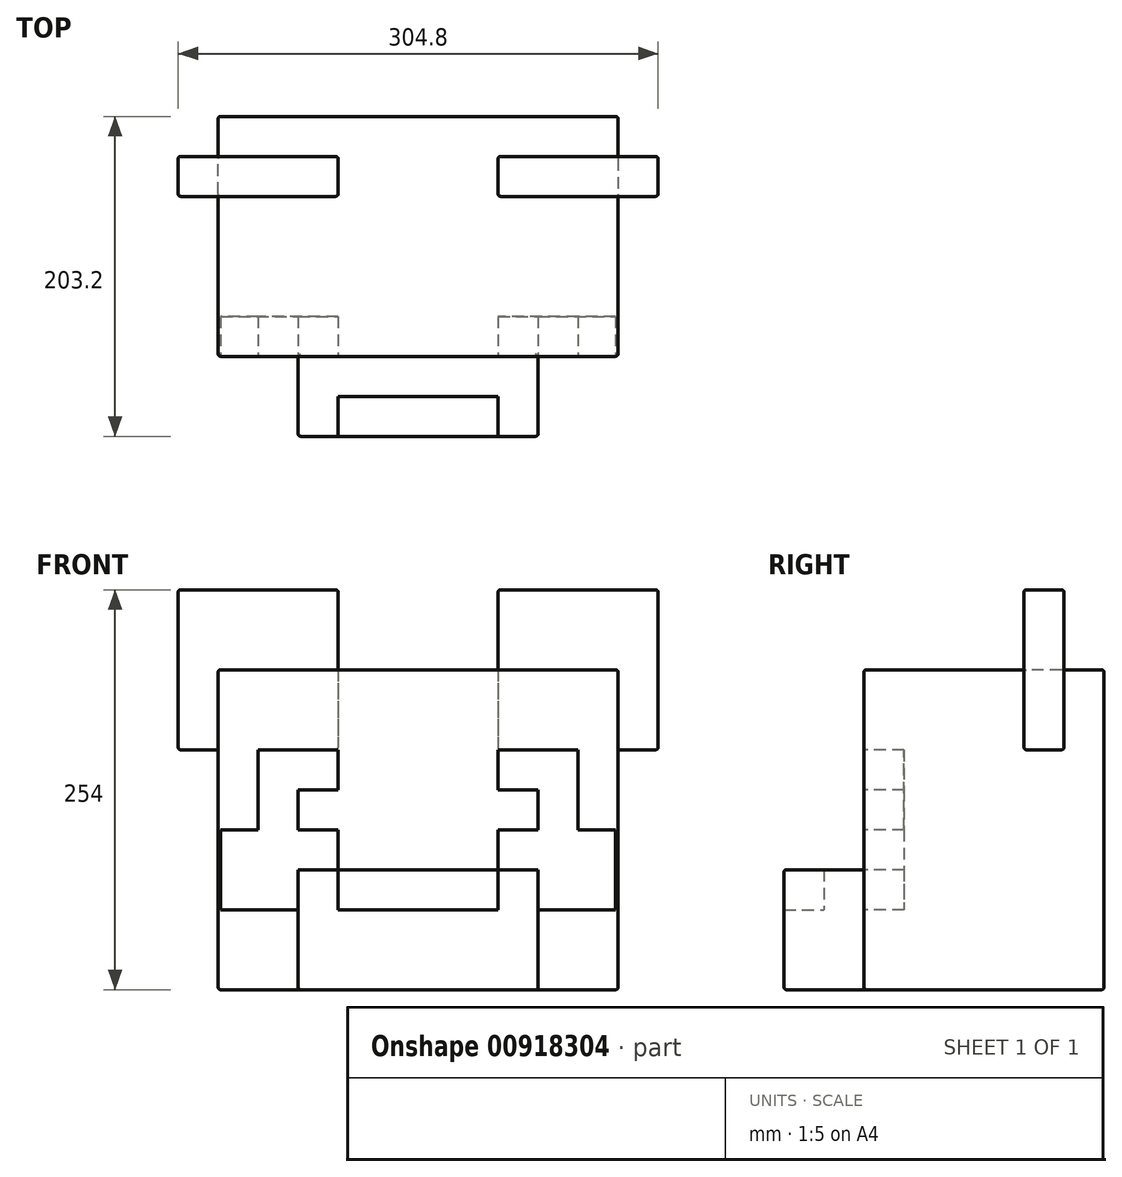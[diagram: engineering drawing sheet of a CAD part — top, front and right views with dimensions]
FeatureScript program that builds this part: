
annotation { "Feature Type Name" : "Feature", "Feature Type Description" : "" }
export const myFeature = defineFeature(function(context is Context, id is Id, definition is map)
    precondition{}
    {
        {
            var Q0;
            Q0=qCreatedBy(makeId("Front.planeOp"),FACE);
            var sketch = newSketch(context, id + "F0", { "sketchPlane" : qUnion([Q0])});
            skLineSegment(sketch, "E0", {"start": v(50.8, 50.8) * mm, "end": v(50.8, 25.4) * mm});
            skLineSegment(sketch, "E1", {"start": v(50.8, 25.4) * mm, "end": v(76.2, 25.4) * mm});
            skLineSegment(sketch, "E2", {"start": v(76.2, 25.4) * mm, "end": v(76.2, 0) * mm});
            skLineSegment(sketch, "E3.bottom", {"start": v(127, 101.6) * mm, "end": v(-127, 101.6) * mm});
            skLineSegment(sketch, "E3.top", {"start": v(127, -101.6) * mm, "end": v(-127, -101.6) * mm});
            skLineSegment(sketch, "E3.left", {"start": v(127, 101.6) * mm, "end": v(127, -101.6) * mm});
            skLineSegment(sketch, "E3.right", {"start": v(-127, 101.6) * mm, "end": v(-127, -101.6) * mm});
            skPoint(sketch, "E3.middle", {"position": v(0, 0) * mm});
            skPoint(sketch, "E4", {"position": v(127, 76.2) * mm});
            skPoint(sketch, "E5", {"position": v(127, 50.8) * mm});
            skPoint(sketch, "E6", {"position": v(127, 25.4) * mm});
            skPoint(sketch, "E7", {"position": v(127, 0) * mm});
            skPoint(sketch, "E8", {"position": v(127, -25.4) * mm});
            skPoint(sketch, "E9", {"position": v(127, -50.8) * mm});
            skPoint(sketch, "E10", {"position": v(127, -76.2) * mm});
            skPoint(sketch, "E11", {"position": v(76.2, 101.6) * mm});
            skPoint(sketch, "E12", {"position": v(50.8, 101.6) * mm});
            skPoint(sketch, "E13", {"position": v(25.4, 101.6) * mm});
            skPoint(sketch, "E14", {"position": v(0, 101.6) * mm});
            skPoint(sketch, "E15", {"position": v(-50.8, 101.6) * mm});
            skPoint(sketch, "E16", {"position": v(-76.2, 101.6) * mm});
            skPoint(sketch, "E17", {"position": v(-101.6, 101.6) * mm});
            skLineSegment(sketch, "E18", {"start": v(50.8, 50.8) * mm, "end": v(101.6, 50.8) * mm});
            skLineSegment(sketch, "E19", {"start": v(76.2, 0) * mm, "end": v(50.8, 0) * mm});
            skLineSegment(sketch, "E20", {"start": v(50.8, 0) * mm, "end": v(50.8, -25.4) * mm});
            skLineSegment(sketch, "E21", {"start": v(50.8, -25.4) * mm, "end": v(76.2, -25.4) * mm});
            skLineSegment(sketch, "E22", {"start": v(76.2, -25.4) * mm, "end": v(76.2, -50.8) * mm});
            skLineSegment(sketch, "E23", {"start": v(76.2, -50.8) * mm, "end": v(127, -50.8) * mm});
            skLineSegment(sketch, "E24", {"start": v(101.6, 50.8) * mm, "end": v(101.6, 0) * mm});
            skLineSegment(sketch, "E25", {"start": v(76.2, -50.8) * mm, "end": v(76.2, -101.6) * mm});
            skLineSegment(sketch, "E26", {"start": v(0, 101.6) * mm, "end": v(0, -101.6) * mm, "construction": true});
            skLineSegment(sketch, "E27.MirrorCS", {"start": v(-76.2, -25.4) * mm, "end": v(-76.2, -50.8) * mm});
            skLineSegment(sketch, "E28.MirrorCS", {"start": v(-50.8, 50.8) * mm, "end": v(-101.6, 50.8) * mm});
            skLineSegment(sketch, "E29.MirrorCS", {"start": v(-76.2, -50.8) * mm, "end": v(-127, -50.8) * mm});
            skLineSegment(sketch, "E30.MirrorCS", {"start": v(-50.8, 0) * mm, "end": v(-50.8, -25.4) * mm});
            skLineSegment(sketch, "E31.MirrorCS", {"start": v(-101.6, 50.8) * mm, "end": v(-101.6, 0) * mm});
            skLineSegment(sketch, "E32.MirrorCS", {"start": v(-50.8, -25.4) * mm, "end": v(-76.2, -25.4) * mm});
            skLineSegment(sketch, "E33.MirrorCS", {"start": v(-50.8, 25.4) * mm, "end": v(-76.2, 25.4) * mm});
            skLineSegment(sketch, "E34.MirrorCS", {"start": v(-76.2, 0) * mm, "end": v(-50.8, 0) * mm});
            skLineSegment(sketch, "E35.MirrorCS", {"start": v(-76.2, -50.8) * mm, "end": v(-76.2, -101.6) * mm});
            skLineSegment(sketch, "E36.MirrorCS", {"start": v(-50.8, 50.8) * mm, "end": v(-50.8, 25.4) * mm});
            skLineSegment(sketch, "E37.MirrorCS", {"start": v(-76.2, 25.4) * mm, "end": v(-76.2, 0) * mm});
            skLineSegment(sketch, "E38", {"start": v(-50.8, -25.4) * mm, "end": v(50.8, -25.4) * mm});
            skPoint(sketch, "E39.MirrorCS.end.orphan", {"position": v(-127, 25.4) * mm});
            skLineSegment(sketch, "E40", {"start": v(101.6, 0) * mm, "end": v(127, 0) * mm});
            skLineSegment(sketch, "E41.MirrorCS", {"start": v(-101.6, 0) * mm, "end": v(-127, 0) * mm});
            skPoint(sketch, "E42", {"position": v(101.6, 101.6) * mm});
            skPoint(sketch, "E43", {"position": v(-25.4, 101.6) * mm});
            skSolve(sketch);
        }
        {
            var Q0;
            Q0=makeQuery(id+"F0.imprint","IMPRINT",FACE,{"disambiguationData":[TD([[makeQuery(id+"F0.imprint","IMPRINT",EDGE,{"derivedFrom":sQuery(id+"F0.wireOp",EDGE,"E0")}),-1.0]])]});
            var Q1;
            Q1=makeQuery(id+"F0.imprint","IMPRINT",FACE,{"disambiguationData":[TD([[makeQuery(id+"F0.imprint","IMPRINT",EDGE,{"derivedFrom":sQuery(id+"F0.wireOp",EDGE,"E28.MirrorCS")}),1.0]])]});
            var Q2;
            Q2=makeQuery(id+"F0.imprint","IMPRINT",FACE,{"disambiguationData":[TD([[makeQuery(id+"F0.imprint","IMPRINT",EDGE,{"derivedFrom":sQuery(id+"F0.wireOp",EDGE,"E0")}),1.0]])]});
            var Q3;
            Q3=makeQuery(id+"F0.imprint","IMPRINT",FACE,{"disambiguationData":[TD([[makeQuery(id+"F0.imprint","IMPRINT",EDGE,{"derivedFrom":sQuery(id+"F0.wireOp",EDGE,"E27.MirrorCS")}),-1.0]])]});
            var Q4;
            Q4=makeQuery(id+"F0.imprint","IMPRINT",FACE,{"disambiguationData":[TD([[makeQuery(id+"F0.imprint","IMPRINT",EDGE,{"derivedFrom":sQuery(id+"F0.wireOp",EDGE,"E2")}),1.0]])]});
            var Q5;
            {var subQ4=sQuery(id+"F0.wireOp",EDGE,"E29.MirrorCS");Q5=makeQuery(id+"F0.imprint","IMPRINT",FACE,{"disambiguationData":[TD([[makeQuery(id+"F0.imprint","IMPRINT",EDGE,{"derivedFrom":subQ4}),1.0]])]});}
            var Q6;
            Q6=makeQuery(id+"F0.imprint","IMPRINT",FACE,{"disambiguationData":[TD([[makeQuery(id+"F0.imprint","IMPRINT",EDGE,{"derivedFrom":sQuery(id+"F0.wireOp",EDGE,"E21")}),-1.0]])]});
            var Q7;
            {var subQ4=sQuery(id+"F0.wireOp",EDGE,"E23");Q7=makeQuery(id+"F0.imprint","IMPRINT",FACE,{"disambiguationData":[TD([[makeQuery(id+"F0.imprint","IMPRINT",EDGE,{"derivedFrom":subQ4}),-1.0]])]});}
            extrude(context, id + "F1", {"entities" : qUnion([Q0, Q1, Q2, Q3, Q4, Q5, Q6, Q7]), "oppositeDirection" : true, "depth" : 152.4 * mm, "offsetDistance" : 25.4 * mm});
        }
        {
            var Q0;
            Q0=makeQuery(id+"F0.imprint","IMPRINT",FACE,{"disambiguationData":[TD([[makeQuery(id+"F0.imprint","IMPRINT",EDGE,{"derivedFrom":sQuery(id+"F0.wireOp",EDGE,"E21")}),-1.0]])]});
            extrude(context, id + "F2", {"entities" : qUnion([Q0]), "operationType" : NewBodyOperationType.ADD, "depth" : 50.8 * mm, "offsetDistance" : 25.4 * mm});
        }
        {
            var Q0;
            Q0=makeQuery(id+"F2.opExtrude","CAP_FACE",FACE,{"disambiguationData":[OSD([sQuery(id+"F0.wireOp",EDGE,"E3.top"),sQuery(id+"F0.wireOp",EDGE,"E21"),sQuery(id+"F0.wireOp",EDGE,"E22"),sQuery(id+"F0.wireOp",EDGE,"E25"),sQuery(id+"F0.wireOp",EDGE,"E27.MirrorCS"),sQuery(id+"F0.wireOp",EDGE,"E32.MirrorCS"),sQuery(id+"F0.wireOp",EDGE,"E35.MirrorCS"),sQuery(id+"F0.wireOp",EDGE,"E38")])],"isStart":false});
            var sketch = newSketch(context, id + "F3", { "sketchPlane" : qUnion([Q0])});
            skLineSegment(sketch, "E44", {"start": v(-50.8, -25.4) * mm, "end": v(50.8, -25.4) * mm});
            skLineSegment(sketch, "E45", {"start": v(50.8, -25.4) * mm, "end": v(50.8, -50.8) * mm});
            skLineSegment(sketch, "E46", {"start": v(50.8, -50.8) * mm, "end": v(-50.8, -50.8) * mm});
            skLineSegment(sketch, "E47", {"start": v(-50.8, -50.8) * mm, "end": v(-50.8, -25.4) * mm});
            skSolve(sketch);
        }
        {
            var Q0;
            Q0=makeQuery(id+"F3.imprint","IMPRINT",FACE,{"disambiguationData":[TD([[makeQuery(id+"F3.imprint","IMPRINT",EDGE,{"derivedFrom":sQuery(id+"F3.wireOp",EDGE,"E44")}),-1.0]])]});
            extrude(context, id + "F4", {"entities" : qUnion([Q0]), "operationType" : NewBodyOperationType.REMOVE, "oppositeDirection" : true, "depth" : 25.4 * mm, "offsetDistance" : 25.4 * mm});
        }
        {
            var Q0;
            Q0=makeQuery(id+"F4.boolean.opBoolean","COPY",FACE,{"derivedFrom":makeQuery(id+"F4.opExtrude","CAP_FACE",FACE,{"disambiguationData":[OSD([sQuery(id+"F3.wireOp",EDGE,"E44"),sQuery(id+"F3.wireOp",EDGE,"E45"),sQuery(id+"F3.wireOp",EDGE,"E46"),sQuery(id+"F3.wireOp",EDGE,"E47")])],"isStart":false})});
            extrude(context, id + "F5", {"entities" : qUnion([Q0]), "depth" : 25.4 * mm, "offsetDistance" : 25.4 * mm});
        }
        {
            var Q0;
            Q0=qCreatedBy(makeId("Front.planeOp"),FACE);
            cPlane(context, id + "F6", {"entities" : qUnion([Q0]), "cplaneType" : CPlaneType.OFFSET, "offset" : 101.6 * mm, "oppositeDirection" : true, "width" : 152.4 * mm, "height" : 152.4 * mm});
        }
        {
            var Q0;
            Q0=qCreatedBy(id+"F6.planeOp",FACE);
            var sketch = newSketch(context, id + "F7", { "sketchPlane" : qUnion([Q0])});
            skLineSegment(sketch, "E48", {"start": v(50.8, 101.6) * mm, "end": v(50.8, 152.4) * mm});
            skLineSegment(sketch, "E49", {"start": v(50.8, 152.4) * mm, "end": v(152.4, 152.4) * mm});
            skLineSegment(sketch, "E50", {"start": v(152.4, 152.4) * mm, "end": v(152.4, 50.8) * mm});
            skLineSegment(sketch, "E51", {"start": v(152.4, 50.8) * mm, "end": v(127, 50.8) * mm});
            skLineSegment(sketch, "E52", {"start": v(127, 50.8) * mm, "end": v(127, 101.6) * mm});
            skLineSegment(sketch, "E53", {"start": v(127, 101.6) * mm, "end": v(50.8, 101.6) * mm});
            skLineSegment(sketch, "E54", {"start": v(50.8, 101.6) * mm, "end": v(50.8, 50.8) * mm});
            skLineSegment(sketch, "E55", {"start": v(50.8, 50.8) * mm, "end": v(127, 50.8) * mm});
            skLineSegment(sketch, "E56.MirrorCS", {"start": v(-50.8, 50.8) * mm, "end": v(-127, 50.8) * mm});
            skLineSegment(sketch, "E57.MirrorCS", {"start": v(-50.8, 101.6) * mm, "end": v(-50.8, 50.8) * mm});
            skLineSegment(sketch, "E58.MirrorCS", {"start": v(-50.8, 101.6) * mm, "end": v(-50.8, 152.4) * mm});
            skLineSegment(sketch, "E59.MirrorCS", {"start": v(-50.8, 152.4) * mm, "end": v(-152.4, 152.4) * mm});
            skLineSegment(sketch, "E60.MirrorCS", {"start": v(-152.4, 152.4) * mm, "end": v(-152.4, 50.8) * mm});
            skLineSegment(sketch, "E61.MirrorCS", {"start": v(-152.4, 50.8) * mm, "end": v(-127, 50.8) * mm});
            skSolve(sketch);
        }
        {
            var Q0;
            Q0=makeQuery(id+"F7.imprint","IMPRINT",FACE,{"disambiguationData":[TD([[makeQuery(id+"F7.imprint","IMPRINT",EDGE,{"derivedFrom":sQuery(id+"F7.wireOp",EDGE,"E52")}),1.0]])]});
            var Q1;
            Q1=makeQuery(id+"F7.imprint","IMPRINT",FACE,{"disambiguationData":[TD([[makeQuery(id+"F7.imprint","IMPRINT",EDGE,{"derivedFrom":sQuery(id+"F7.wireOp",EDGE,"E48")}),-1.0]])]});
            var Q2;
            Q2=makeQuery(id+"F7.imprint","IMPRINT",FACE,{"disambiguationData":[TD([[makeQuery(id+"F7.imprint","IMPRINT",EDGE,{"derivedFrom":sQuery(id+"F7.wireOp",EDGE,"E56.MirrorCS")}),-1.0]])]});
            extrude(context, id + "F8", {"entities" : qUnion([Q0, Q1, Q2]), "oppositeDirection" : true, "depth" : 25.4 * mm, "offsetDistance" : 25.4 * mm});
        }
        {
            var Q0;
            {var subQ0=sQuery(id+"F0.wireOp",EDGE,"E38");var subQ2=sQuery(id+"F0.wireOp",EDGE,"E32.MirrorCS");var subQ4=sQuery(id+"F0.wireOp",EDGE,"E21");Q0=makeQuery(id+"F4.boolean.opBoolean","SPLIT",EDGE,{"disambiguationData":[TD([makeQuery(id+"F4.opExtrude","SWEPT_FACE",FACE,{"disambiguationData":[OSD([sQuery(id+"F3.wireOp",EDGE,"E47")])]})])],"derivedFrom":makeQuery(id+"F2.opExtrude","CAP_EDGE",EDGE,{"disambiguationData":[OSD([subQ4,subQ2,subQ0])],"isStart":false})});}
            var Q1;
            Q1=makeQuery(id+"F5.opExtrude","CAP_EDGE",EDGE,{"disambiguationData":[OSD([sQuery(id+"F3.wireOp",EDGE,"E44")])],"isStart":false});
            var Q2;
            {var subQ0=sQuery(id+"F0.wireOp",EDGE,"E38");var subQ1=sQuery(id+"F0.wireOp",EDGE,"E32.MirrorCS");var subQ4=sQuery(id+"F0.wireOp",EDGE,"E21");Q2=makeQuery(id+"F4.boolean.opBoolean","SPLIT",EDGE,{"disambiguationData":[TD([makeQuery(id+"F4.opExtrude","SWEPT_FACE",FACE,{"disambiguationData":[OSD([sQuery(id+"F3.wireOp",EDGE,"E45")])]})])],"derivedFrom":makeQuery(id+"F2.opExtrude","CAP_EDGE",EDGE,{"disambiguationData":[OSD([subQ4,subQ1,subQ0])],"isStart":false})});}
            var Q3;
            {var subQ0=sQuery(id+"F0.wireOp",EDGE,"E3.top");Q3=makeQuery(id+"F2.boolean.opBoolean","MERGE",FACE,{"derivedFrom":[makeQuery(id+"F1.opExtrude","SWEPT_FACE",FACE,{"disambiguationData":[OSD([subQ0])]}),makeQuery(id+"F2.opExtrude","SWEPT_FACE",FACE,{"disambiguationData":[OSD([subQ0])]})]});}
            var Q4;
            Q4=makeQuery(id+"F1.opExtrude","CAP_FACE",FACE,{"disambiguationData":[OSD([sQuery(id+"F0.wireOp",EDGE,"E3.bottom"),sQuery(id+"F0.wireOp",EDGE,"E3.top"),sQuery(id+"F0.wireOp",EDGE,"E3.left"),sQuery(id+"F0.wireOp",EDGE,"E3.right")])],"isStart":false});
            var Q5;
            {var subQ0=sQuery(id+"F0.wireOp",EDGE,"E3.bottom");var subQ1=sQuery(id+"F0.wireOp",EDGE,"E3.right");Q5=makeQuery(id+"F5OZuFi827c7V8s_2.boolean.opBoolean","SPLIT",EDGE,{"disambiguationData":[TD([makeQuery(id+"F1.opExtrude","CAP_FACE",FACE,{"disambiguationData":[OSD([subQ0,sQuery(id+"F0.wireOp",EDGE,"E3.top"),sQuery(id+"F0.wireOp",EDGE,"E3.left"),subQ1])],"isStart":false})])],"derivedFrom":makeQuery(id+"F1.opExtrude","SWEPT_EDGE",EDGE,{"disambiguationData":[OSD([subQ0,subQ1])]})});}
            var Q6;
            {var subQ0=sQuery(id+"F0.wireOp",EDGE,"E3.bottom");var subQ1=sQuery(id+"F0.wireOp",EDGE,"E3.right");Q6=makeQuery(id+"F5OZuFi827c7V8s_2.boolean.opBoolean","SPLIT",EDGE,{"disambiguationData":[TD([makeQuery(id+"F1.opExtrude","CAP_FACE",FACE,{"disambiguationData":[OSD([subQ0,sQuery(id+"F0.wireOp",EDGE,"E3.top"),sQuery(id+"F0.wireOp",EDGE,"E3.left"),subQ1])],"isStart":true})])],"derivedFrom":makeQuery(id+"F1.opExtrude","SWEPT_EDGE",EDGE,{"disambiguationData":[OSD([subQ0,subQ1])]})});}
            var Q7;
            {var subQ0=sQuery(id+"F0.wireOp",EDGE,"E3.bottom");var subQ1=sQuery(id+"F0.wireOp",EDGE,"E3.left");Q7=makeQuery(id+"F5OZuFi827c7V8s_2.boolean.opBoolean","SPLIT",EDGE,{"disambiguationData":[TD([makeQuery(id+"F1.opExtrude","CAP_FACE",FACE,{"disambiguationData":[OSD([subQ0,sQuery(id+"F0.wireOp",EDGE,"E3.top"),subQ1,sQuery(id+"F0.wireOp",EDGE,"E3.right")])],"isStart":false})])],"derivedFrom":makeQuery(id+"F1.opExtrude","SWEPT_EDGE",EDGE,{"disambiguationData":[OSD([subQ0,subQ1])]})});}
            var Q8;
            {var subQ0=sQuery(id+"F0.wireOp",EDGE,"E3.bottom");var subQ1=sQuery(id+"F0.wireOp",EDGE,"E3.left");Q8=makeQuery(id+"F5OZuFi827c7V8s_2.boolean.opBoolean","SPLIT",EDGE,{"disambiguationData":[TD([makeQuery(id+"F1.opExtrude","CAP_FACE",FACE,{"disambiguationData":[OSD([subQ0,sQuery(id+"F0.wireOp",EDGE,"E3.top"),subQ1,sQuery(id+"F0.wireOp",EDGE,"E3.right")])],"isStart":true})])],"derivedFrom":makeQuery(id+"F1.opExtrude","SWEPT_EDGE",EDGE,{"disambiguationData":[OSD([subQ0,subQ1])]})});}
            var Q9;
            Q9=makeQuery(id+"F8.opExtrude","CAP_FACE",FACE,{"disambiguationData":[OSD([sQuery(id+"F7.wireOp",EDGE,"E48"),sQuery(id+"F7.wireOp",EDGE,"E49"),sQuery(id+"F7.wireOp",EDGE,"E50"),sQuery(id+"F7.wireOp",EDGE,"E51"),sQuery(id+"F7.wireOp",EDGE,"E54"),sQuery(id+"F7.wireOp",EDGE,"E55")])],"isStart":true});
            var Q10;
            Q10=makeQuery(id+"F8.opExtrude","CAP_FACE",FACE,{"disambiguationData":[OSD([sQuery(id+"F7.wireOp",EDGE,"E48"),sQuery(id+"F7.wireOp",EDGE,"E49"),sQuery(id+"F7.wireOp",EDGE,"E50"),sQuery(id+"F7.wireOp",EDGE,"E51"),sQuery(id+"F7.wireOp",EDGE,"E54"),sQuery(id+"F7.wireOp",EDGE,"E55")])],"isStart":false});
            var Q11;
            Q11=makeQuery(id+"F8.opExtrude","SWEPT_FACE",FACE,{"disambiguationData":[OSD([sQuery(id+"F7.wireOp",EDGE,"E51"),sQuery(id+"F7.wireOp",EDGE,"E55")])]});
            var Q12;
            Q12=makeQuery(id+"F8.opExtrude","SWEPT_FACE",FACE,{"disambiguationData":[OSD([sQuery(id+"F7.wireOp",EDGE,"E49")])]});
            var Q13;
            Q13=makeQuery(id+"F8.opExtrude","CAP_FACE",FACE,{"disambiguationData":[OSD([sQuery(id+"F7.wireOp",EDGE,"E56.MirrorCS"),sQuery(id+"F7.wireOp",EDGE,"E57.MirrorCS"),sQuery(id+"F7.wireOp",EDGE,"E58.MirrorCS"),sQuery(id+"F7.wireOp",EDGE,"E59.MirrorCS"),sQuery(id+"F7.wireOp",EDGE,"E60.MirrorCS"),sQuery(id+"F7.wireOp",EDGE,"E61.MirrorCS")])],"isStart":false});
            var Q14;
            Q14=makeQuery(id+"F8.opExtrude","CAP_FACE",FACE,{"disambiguationData":[OSD([sQuery(id+"F7.wireOp",EDGE,"E56.MirrorCS"),sQuery(id+"F7.wireOp",EDGE,"E57.MirrorCS"),sQuery(id+"F7.wireOp",EDGE,"E58.MirrorCS"),sQuery(id+"F7.wireOp",EDGE,"E59.MirrorCS"),sQuery(id+"F7.wireOp",EDGE,"E60.MirrorCS"),sQuery(id+"F7.wireOp",EDGE,"E61.MirrorCS")])],"isStart":true});
            var Q15;
            Q15=makeQuery(id+"F8.opExtrude","SWEPT_FACE",FACE,{"disambiguationData":[OSD([sQuery(id+"F7.wireOp",EDGE,"E56.MirrorCS"),sQuery(id+"F7.wireOp",EDGE,"E61.MirrorCS")])]});
            var Q16;
            Q16=makeQuery(id+"F8.opExtrude","SWEPT_FACE",FACE,{"disambiguationData":[OSD([sQuery(id+"F7.wireOp",EDGE,"E59.MirrorCS")])]});
            var Q17;
            Q17=makeQuery(id+"F2.opExtrude","CAP_EDGE",EDGE,{"disambiguationData":[OSD([sQuery(id+"F0.wireOp",EDGE,"E22"),sQuery(id+"F0.wireOp",EDGE,"E25")])],"isStart":false});
            var Q18;
            Q18=makeQuery(id+"F2.opExtrude","SWEPT_EDGE",EDGE,{"disambiguationData":[OSD([sQuery(id+"F0.wireOp",EDGE,"E21"),sQuery(id+"F0.wireOp",EDGE,"E22")])]});
            var Q19;
            Q19=makeQuery(id+"F2.opExtrude","CAP_EDGE",EDGE,{"disambiguationData":[OSD([sQuery(id+"F0.wireOp",EDGE,"E27.MirrorCS"),sQuery(id+"F0.wireOp",EDGE,"E35.MirrorCS")])],"isStart":false});
            var Q20;
            Q20=makeQuery(id+"F2.opExtrude","SWEPT_EDGE",EDGE,{"disambiguationData":[OSD([sQuery(id+"F0.wireOp",EDGE,"E27.MirrorCS"),sQuery(id+"F0.wireOp",EDGE,"E32.MirrorCS")])]});
            var Q21;
            Q21=makeQuery(id+"F1.opExtrude","CAP_EDGE",EDGE,{"disambiguationData":[OSD([sQuery(id+"F0.wireOp",EDGE,"E3.left")])],"isStart":true});
            var Q22;
            Q22=makeQuery(id+"F1.opExtrude","CAP_EDGE",EDGE,{"disambiguationData":[OSD([sQuery(id+"F0.wireOp",EDGE,"E3.bottom")])],"isStart":true});
            var Q23;
            Q23=makeQuery(id+"F1.opExtrude","CAP_EDGE",EDGE,{"disambiguationData":[OSD([sQuery(id+"F0.wireOp",EDGE,"E3.right")])],"isStart":true});
            fillet(context, id + "F9", {"entities" : qUnion([Q0, Q1, Q2, Q3, Q4, Q5, Q6, Q7, Q8, Q9, Q10, Q11, Q12, Q13, Q14, Q15, Q16, Q17, Q18, Q19, Q20, Q21, Q22, Q23]), "radius" : 1.52 * mm, "tangentPropagation" : true, "allowEdgeOverflow" : false});
        }
        {
            var Q0;
            Q0=makeQuery(id+"F8.opExtrude","SWEPT_BODY",BODY,{"disambiguationData":[OSD([sQuery(id+"F7.wireOp",EDGE,"E48"),sQuery(id+"F7.wireOp",EDGE,"E49"),sQuery(id+"F7.wireOp",EDGE,"E50"),sQuery(id+"F7.wireOp",EDGE,"E51"),sQuery(id+"F7.wireOp",EDGE,"E54"),sQuery(id+"F7.wireOp",EDGE,"E55")])]});
            var Q1;
            Q1=makeQuery(id+"F8.opExtrude","SWEPT_BODY",BODY,{"disambiguationData":[OSD([sQuery(id+"F7.wireOp",EDGE,"E56.MirrorCS"),sQuery(id+"F7.wireOp",EDGE,"E57.MirrorCS"),sQuery(id+"F7.wireOp",EDGE,"E58.MirrorCS"),sQuery(id+"F7.wireOp",EDGE,"E59.MirrorCS"),sQuery(id+"F7.wireOp",EDGE,"E60.MirrorCS"),sQuery(id+"F7.wireOp",EDGE,"E61.MirrorCS")])]});
            var Q2;
            Q2=makeQuery(id+"F1.opExtrude","SWEPT_BODY",BODY,{"disambiguationData":[OSD([sQuery(id+"F0.wireOp",EDGE,"E3.bottom"),sQuery(id+"F0.wireOp",EDGE,"E3.top"),sQuery(id+"F0.wireOp",EDGE,"E3.left"),sQuery(id+"F0.wireOp",EDGE,"E3.right")])]});
            booleanBodies(context, id + "F10", {"operationType" : BooleanOperationType.SUBTRACTION, "tools" : qUnion([Q0, Q1]), "targets" : qUnion([Q2]), "keepTools" : true});
        }
        {
            var Q0;
            Q0=qCreatedBy(makeId("Front.planeOp"),FACE);
            var sketch = newSketch(context, id + "F11", { "sketchPlane" : qUnion([Q0])});
            skLineSegment(sketch, "E62.0.0", {"start": v(-101.6, 0) * mm, "end": v(-125.48, 0) * mm});
            skLineSegment(sketch, "E62.0.2", {"start": v(-125.48, -50.8) * mm, "end": v(-76.2, -50.8) * mm});
            skLineSegment(sketch, "E62.0.3", {"start": v(-76.2, -50.8) * mm, "end": v(-76.2, -25.4) * mm});
            skLineSegment(sketch, "E62.0.4", {"start": v(-76.2, -25.4) * mm, "end": v(-50.8, -25.4) * mm});
            skLineSegment(sketch, "E62.0.5", {"start": v(-50.8, -25.4) * mm, "end": v(-50.8, 0) * mm});
            skLineSegment(sketch, "E62.0.6", {"start": v(-50.8, 0) * mm, "end": v(-76.2, 0) * mm});
            skLineSegment(sketch, "E62.0.7", {"start": v(-76.2, 0) * mm, "end": v(-76.2, 25.4) * mm});
            skLineSegment(sketch, "E62.0.8", {"start": v(-76.2, 25.4) * mm, "end": v(-50.8, 25.4) * mm});
            skLineSegment(sketch, "E62.0.9", {"start": v(-50.8, 25.4) * mm, "end": v(-50.8, 50.8) * mm});
            skLineSegment(sketch, "E62.0.10", {"start": v(-50.8, 50.8) * mm, "end": v(-101.6, 50.8) * mm});
            skLineSegment(sketch, "E62.0.11", {"start": v(-101.6, 50.8) * mm, "end": v(-101.6, 0) * mm});
            skLineSegment(sketch, "E63.0.1", {"start": v(125.48, 0) * mm, "end": v(101.6, 0) * mm});
            skLineSegment(sketch, "E63.0.2", {"start": v(101.6, 0) * mm, "end": v(101.6, 50.8) * mm});
            skLineSegment(sketch, "E63.0.3", {"start": v(101.6, 50.8) * mm, "end": v(50.8, 50.8) * mm});
            skLineSegment(sketch, "E63.0.4", {"start": v(50.8, 50.8) * mm, "end": v(50.8, 25.4) * mm});
            skLineSegment(sketch, "E63.0.5", {"start": v(50.8, 25.4) * mm, "end": v(76.2, 25.4) * mm});
            skLineSegment(sketch, "E63.0.6", {"start": v(76.2, 25.4) * mm, "end": v(76.2, 0) * mm});
            skLineSegment(sketch, "E63.0.7", {"start": v(76.2, 0) * mm, "end": v(50.8, 0) * mm});
            skLineSegment(sketch, "E63.0.8", {"start": v(50.8, 0) * mm, "end": v(50.8, -25.4) * mm});
            skLineSegment(sketch, "E63.0.9", {"start": v(50.8, -25.4) * mm, "end": v(76.2, -25.4) * mm});
            skLineSegment(sketch, "E63.0.10", {"start": v(76.2, -25.4) * mm, "end": v(76.2, -50.8) * mm});
            skLineSegment(sketch, "E63.0.11", {"start": v(76.2, -50.8) * mm, "end": v(125.48, -50.8) * mm});
            skLineSegment(sketch, "E64", {"start": v(125.48, 0) * mm, "end": v(125.48, -50.8) * mm});
            skPoint(sketch, "E65.orphan", {"position": v(127, 0) * mm});
            skPoint(sketch, "E66.orphan", {"position": v(127, -50.8) * mm});
            skLineSegment(sketch, "E67", {"start": v(-125.48, 0) * mm, "end": v(-125.48, -50.8) * mm});
            skPoint(sketch, "E68.orphan", {"position": v(-127, 0) * mm});
            skPoint(sketch, "E69.orphan", {"position": v(-127, -50.8) * mm});
            skSolve(sketch);
        }
        {
            var Q0;
            Q0=makeQuery(id+"F11.imprint","IMPRINT",FACE,{"disambiguationData":[TD([[makeQuery(id+"F11.imprint","IMPRINT",EDGE,{"derivedFrom":sQuery(id+"F11.wireOp",EDGE,"E62.0.0")}),1.0]])]});
            var Q1;
            Q1=makeQuery(id+"F11.imprint","IMPRINT",FACE,{"disambiguationData":[TD([[makeQuery(id+"F11.imprint","IMPRINT",EDGE,{"derivedFrom":sQuery(id+"F11.wireOp",EDGE,"E63.0.1")}),1.0]])]});
            extrude(context, id + "F12", {"entities" : qUnion([Q0, Q1]), "operationType" : NewBodyOperationType.REMOVE, "oppositeDirection" : true, "depth" : 25.4 * mm, "offsetDistance" : 25.4 * mm});
        }
        {
            var Q0;
            Q0=makeQuery(id+"F11.imprint","IMPRINT",FACE,{"disambiguationData":[TD([[makeQuery(id+"F11.imprint","IMPRINT",EDGE,{"derivedFrom":sQuery(id+"F11.wireOp",EDGE,"E62.0.0")}),1.0]])]});
            var Q1;
            Q1=makeQuery(id+"F11.imprint","IMPRINT",FACE,{"disambiguationData":[TD([[makeQuery(id+"F11.imprint","IMPRINT",EDGE,{"derivedFrom":sQuery(id+"F11.wireOp",EDGE,"E63.0.1")}),1.0]])]});
            extrude(context, id + "F13", {"entities" : qUnion([Q0, Q1]), "oppositeDirection" : true, "depth" : 25.4 * mm, "offsetDistance" : 25.4 * mm});
        }
    });
